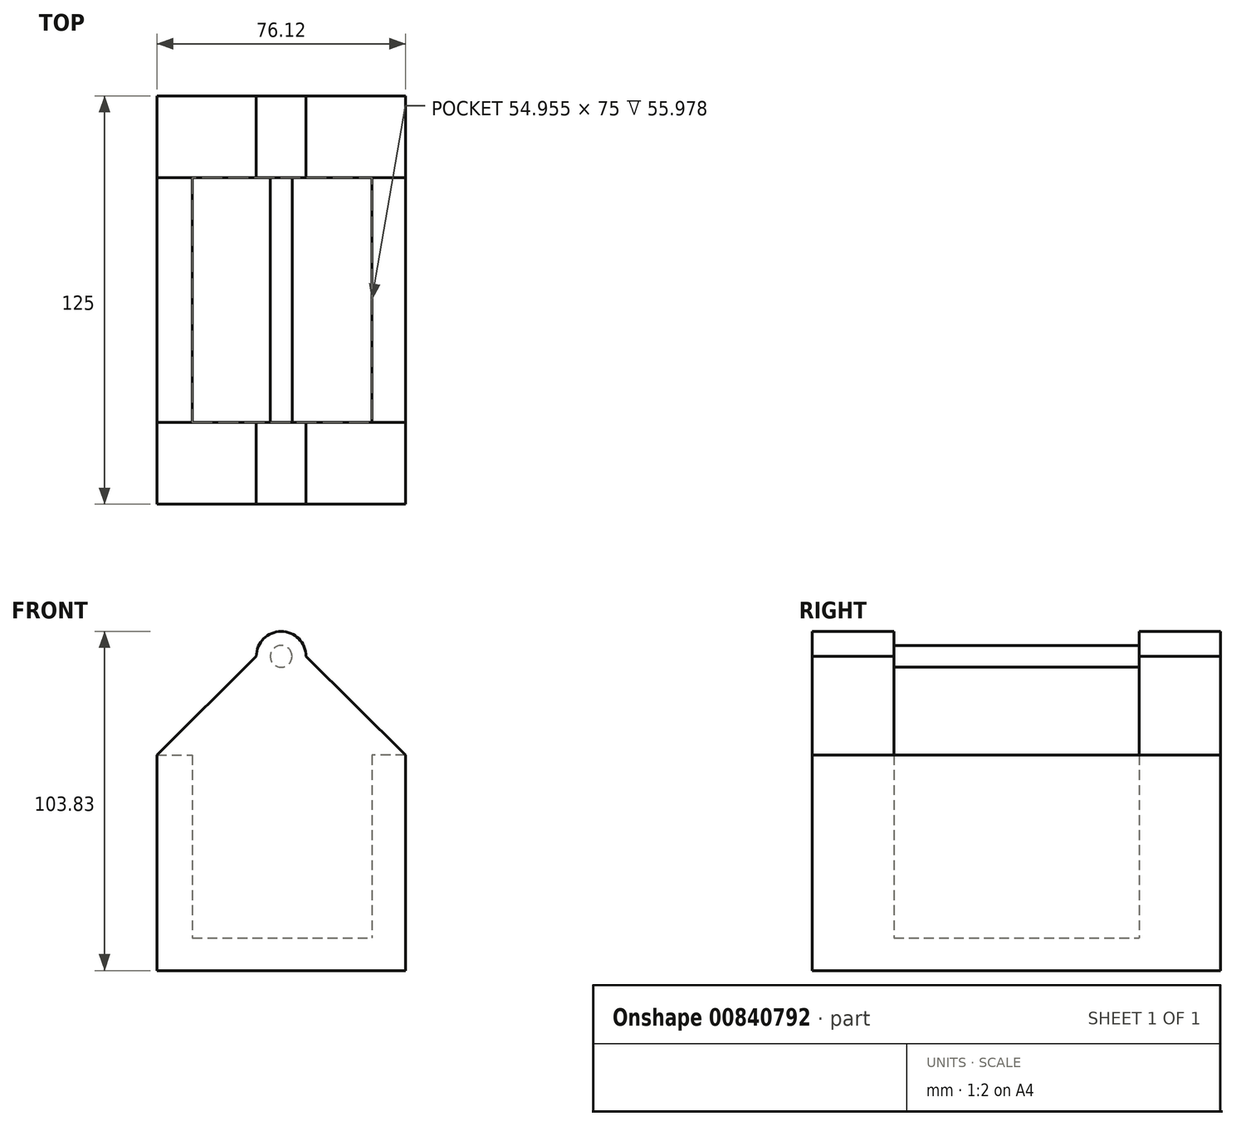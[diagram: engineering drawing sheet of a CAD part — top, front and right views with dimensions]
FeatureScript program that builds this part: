
annotation { "Feature Type Name" : "Feature", "Feature Type Description" : "" }
export const myFeature = defineFeature(function(context is Context, id is Id, definition is map)
    precondition{}
    {
        {
            var Q0;
            Q0=qCreatedBy(makeId("Front.planeOp"),FACE);
            var sketch = newSketch(context, id + "F0", { "sketchPlane" : qUnion([Q0])});
            skLineSegment(sketch, "E0.bottom", {"start": v(0, 0) * mm, "end": v(76.12, 0) * mm});
            skLineSegment(sketch, "E0.top", {"start": v(0, -55.98) * mm, "end": v(76.12, -55.98) * mm});
            skLineSegment(sketch, "E0.left", {"start": v(0, 0) * mm, "end": v(0, -55.98) * mm});
            skLineSegment(sketch, "E0.right", {"start": v(76.12, 0) * mm, "end": v(76.12, -55.98) * mm});
            skLineSegment(sketch, "E1", {"start": v(0, 0) * mm, "end": v(38.06, 0) * mm});
            skLineSegment(sketch, "E2", {"start": v(38.06, 30.23) * mm, "end": v(38.06, 30.28) * mm});
            skLineSegment(sketch, "E3", {"start": v(30.45, 30.28) * mm, "end": v(0, 0) * mm});
            skLineSegment(sketch, "E4", {"start": v(45.68, 30.28) * mm, "end": v(76.12, 0) * mm});
            skArc(sketch, "E5", {"start": v(45.68, 30.28) * mm, "mid": v(38.06, 37.85) * mm, "end": v(30.45, 30.28) * mm});
            skSolve(sketch);
        }
        {
            var Q0;
            Q0 = qSketchRegion(id + "F0", true);
            extrude(context, id + "F1", {"entities" : qUnion([Q0]), "depth" : 25 * mm, "offsetDistance" : 25 * mm});
        }
        {
            var Q0;
            Q0=makeQuery(id+"F1.opExtrude","CAP_FACE",FACE,{"disambiguationData":[OSD([sQuery(id+"F0.wireOp",EDGE,"E0.top"),sQuery(id+"F0.wireOp",EDGE,"E0.left"),sQuery(id+"F0.wireOp",EDGE,"E0.right"),sQuery(id+"F0.wireOp",EDGE,"E3"),sQuery(id+"F0.wireOp",EDGE,"E4"),sQuery(id+"F0.wireOp",EDGE,"E5")])],"isStart":false});
            var sketch = newSketch(context, id + "F2", { "sketchPlane" : qUnion([Q0])});
            skLineSegment(sketch, "E6", {"start": v(0, 0) * mm, "end": v(10.9, 0) * mm});
            skLineSegment(sketch, "E7", {"start": v(10.9, 0) * mm, "end": v(10.9, -55.98) * mm});
            skLineSegment(sketch, "E8", {"start": v(10.9, -55.98) * mm, "end": v(0, -55.98) * mm});
            skLineSegment(sketch, "E9", {"start": v(0, -55.98) * mm, "end": v(0, 0) * mm});
            skLineSegment(sketch, "E10", {"start": v(76.12, 0) * mm, "end": v(65.86, 0) * mm});
            skLineSegment(sketch, "E11", {"start": v(65.86, 0) * mm, "end": v(65.86, -55.98) * mm});
            skLineSegment(sketch, "E12", {"start": v(65.86, -55.98) * mm, "end": v(76.12, -55.98) * mm});
            skLineSegment(sketch, "E13", {"start": v(76.12, -55.98) * mm, "end": v(76.12, 0) * mm});
            skSolve(sketch);
        }
        {
            var Q0;
            Q0 = qSketchRegion(id + "F2", true);
            extrude(context, id + "F3", {"entities" : qUnion([Q0]), "operationType" : NewBodyOperationType.ADD, "depth" : 75 * mm, "offsetDistance" : 25 * mm});
        }
        {
            var Q0;
            Q0=makeQuery(id+"F3.opExtrude","CAP_FACE",FACE,{"disambiguationData":[OSD([sQuery(id+"F2.wireOp",EDGE,"E6"),sQuery(id+"F2.wireOp",EDGE,"E7"),sQuery(id+"F2.wireOp",EDGE,"E8"),sQuery(id+"F2.wireOp",EDGE,"E9")])],"isStart":false});
            var sketch = newSketch(context, id + "F4", { "sketchPlane" : qUnion([Q0])});
            skLineSegment(sketch, "E14.bottom", {"start": v(0, 0) * mm, "end": v(76.12, 0) * mm});
            skLineSegment(sketch, "E14.top", {"start": v(0, -55.98) * mm, "end": v(76.12, -55.98) * mm});
            skLineSegment(sketch, "E14.left", {"start": v(0, 0) * mm, "end": v(0, -55.98) * mm});
            skLineSegment(sketch, "E14.right", {"start": v(76.12, 0) * mm, "end": v(76.12, -55.98) * mm});
            skLineSegment(sketch, "E15", {"start": v(0, 0) * mm, "end": v(38.06, 0) * mm});
            skLineSegment(sketch, "E16", {"start": v(38.06, 30.23) * mm, "end": v(38.06, 30.28) * mm});
            skLineSegment(sketch, "E17", {"start": v(30.45, 30.28) * mm, "end": v(0, 0) * mm});
            skLineSegment(sketch, "E18", {"start": v(45.68, 30.28) * mm, "end": v(76.12, 0) * mm});
            skArc(sketch, "E19", {"start": v(45.68, 30.28) * mm, "mid": v(38.06, 37.85) * mm, "end": v(30.45, 30.28) * mm});
            skSolve(sketch);
        }
        {
            var Q0;
            Q0 = qSketchRegion(id + "F4", true);
            extrude(context, id + "F5", {"entities" : qUnion([Q0]), "operationType" : NewBodyOperationType.ADD, "depth" : 25 * mm, "offsetDistance" : 25 * mm});
        }
        {
            var Q0;
            Q0=makeQuery(id+"F5.opExtrude","CAP_FACE",FACE,{"disambiguationData":[OSD([sQuery(id+"F4.wireOp",EDGE,"E14.top"),sQuery(id+"F4.wireOp",EDGE,"E14.left"),sQuery(id+"F4.wireOp",EDGE,"E14.right"),sQuery(id+"F4.wireOp",EDGE,"E17"),sQuery(id+"F4.wireOp",EDGE,"E18"),sQuery(id+"F4.wireOp",EDGE,"E19")])],"isStart":true});
            var sketch = newSketch(context, id + "F6", { "sketchPlane" : qUnion([Q0])});
            skCircle(sketch, "E20", {"center": v(-38.06, 30.23) * mm, "radius": 3.33 * mm});
            skSolve(sketch);
        }
        {
            var Q0;
            Q0 = qSketchRegion(id + "F6", true);
            extrude(context, id + "F7", {"entities" : qUnion([Q0]), "operationType" : NewBodyOperationType.ADD, "depth" : 89.4 * mm, "offsetDistance" : 25 * mm});
        }
        {
            var Q0;
            Q0=makeQuery(id+"F5.boolean.opBoolean","MERGE",FACE,{"derivedFrom":[makeQuery(id+"F3.boolean.opBoolean","MERGE",FACE,{"derivedFrom":[makeQuery(id+"F1.opExtrude","SWEPT_FACE",FACE,{"disambiguationData":[OSD([sQuery(id+"F0.wireOp",EDGE,"E0.top")])]}),makeQuery(id+"F3.opExtrude","SWEPT_FACE",FACE,{"disambiguationData":[OSD([sQuery(id+"F2.wireOp",EDGE,"E8")])]}),makeQuery(id+"F3.opExtrude","SWEPT_FACE",FACE,{"disambiguationData":[OSD([sQuery(id+"F2.wireOp",EDGE,"E12")])]})]}),makeQuery(id+"F5.opExtrude","SWEPT_FACE",FACE,{"disambiguationData":[OSD([sQuery(id+"F4.wireOp",EDGE,"E14.top")])]})]});
            var sketch = newSketch(context, id + "F8", { "sketchPlane" : qUnion([Q0])});
            skLineSegment(sketch, "E21.bottom", {"start": v(0, 0) * mm, "end": v(76.12, 0) * mm});
            skLineSegment(sketch, "E21.top", {"start": v(0, 125) * mm, "end": v(76.12, 125) * mm});
            skLineSegment(sketch, "E21.left", {"start": v(0, 0) * mm, "end": v(0, 125) * mm});
            skLineSegment(sketch, "E21.right", {"start": v(76.12, 0) * mm, "end": v(76.12, 125) * mm});
            skSolve(sketch);
        }
        {
            var Q0;
            Q0 = qSketchRegion(id + "F8", true);
            extrude(context, id + "F9", {"entities" : qUnion([Q0]), "operationType" : NewBodyOperationType.ADD, "depth" : 10 * mm, "offsetDistance" : 25 * mm});
        }
    });
